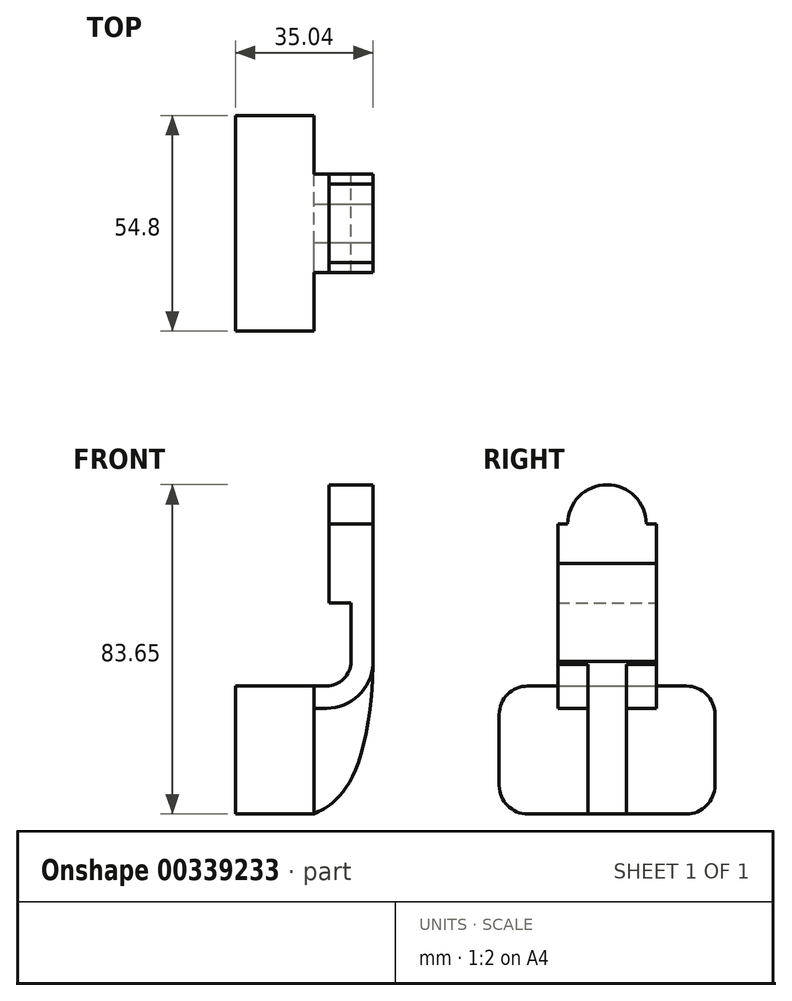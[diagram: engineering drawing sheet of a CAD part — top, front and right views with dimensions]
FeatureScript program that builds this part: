
annotation { "Feature Type Name" : "Feature", "Feature Type Description" : "" }
export const myFeature = defineFeature(function(context is Context, id is Id, definition is map)
    precondition{}
    {
        {
            var Q0;
            Q0=qCreatedBy(makeId("Front.planeOp"),FACE);
            var sketch = newSketch(context, id + "F0", { "sketchPlane" : qUnion([Q0])});
            skLineSegment(sketch, "E0.bottom", {"start": v(-10, 16.25) * mm, "end": v(10, 16.25) * mm});
            skLineSegment(sketch, "E0.top", {"start": v(-10, -16.25) * mm, "end": v(10, -16.25) * mm});
            skLineSegment(sketch, "E0.left", {"start": v(-10, 16.25) * mm, "end": v(-10, -16.25) * mm});
            skLineSegment(sketch, "E0.right", {"start": v(10, 16.25) * mm, "end": v(10, -16.25) * mm});
            skPoint(sketch, "E0.middle", {"position": v(0, 0) * mm});
            skLineSegment(sketch, "E1.bottom", {"start": v(13.75, 57.4) * mm, "end": v(25, 57.4) * mm});
            skLineSegment(sketch, "E1.top", {"start": v(13.75, 37.4) * mm, "end": v(25, 37.4) * mm});
            skLineSegment(sketch, "E1.left", {"start": v(13.75, 57.4) * mm, "end": v(13.75, 37.4) * mm});
            skLineSegment(sketch, "E1.right", {"start": v(25, 57.4) * mm, "end": v(25, 37.4) * mm});
            skPoint(sketch, "E1.middle", {"position": v(19.37, 47.4) * mm});
            skLineSegment(sketch, "E2", {"start": v(10, 16.25) * mm, "end": v(13.13, 16.25) * mm});
            skArc(sketch, "E3", {"start": v(13.13, 16.25) * mm, "mid": v(17.54, 18.08) * mm, "end": v(19.37, 22.5) * mm});
            skLineSegment(sketch, "E4", {"start": v(19.37, 22.5) * mm, "end": v(19.37, 47.4) * mm});
            skLineSegment(sketch, "E5.0", {"start": v(25.04, 22.5) * mm, "end": v(25.04, 47.4) * mm});
            skArc(sketch, "E5.1", {"start": v(13.13, 10.58) * mm, "mid": v(21.55, 14.07) * mm, "end": v(25.04, 22.5) * mm});
            skLineSegment(sketch, "E5.2", {"start": v(10, 10.58) * mm, "end": v(13.13, 10.58) * mm});
            skLineSegment(sketch, "E6", {"start": v(13.75, 47.4) * mm, "end": v(25.04, 47.4) * mm});
            skFitSpline(sketch, "E7", {"points": [v(10, -16.25) * mm, v(25.04, 22.5) * mm], "startDerivative": vector(11.57, 6.62) * mm, "endDerivative": vector(2.78, 102.06) * mm});
            skSolve(sketch);
        }
        {
            var Q0;
            {var subQ1=sQuery(id+"F0.wireOp",EDGE,"E0.bottom");Q0=makeQuery(id+"F0.imprint","IMPRINT",FACE,{"disambiguationData":[TD([[makeQuery(id+"F0.imprint","IMPRINT",EDGE,{"derivedFrom":subQ1}),-1.0]])]});}
            extrude(context, id + "F1", {"entities" : qUnion([Q0]), "endBound" : BoundingType.SYMMETRIC, "depth" : 54.8 * mm});
        }
        {
            var Q0;
            {var subQ9=sQuery(id+"F0.wireOp",EDGE,"E2");Q0=makeQuery(id+"F0.imprint","IMPRINT",FACE,{"disambiguationData":[TD([[makeQuery(id+"F0.imprint","IMPRINT",EDGE,{"derivedFrom":subQ9}),-1.0]])]});}
            var Q1;
            {var subQ1=sQuery(id+"F0.wireOp",EDGE,"E1.bottom");Q1=makeQuery(id+"F0.imprint","IMPRINT",FACE,{"disambiguationData":[TD([[makeQuery(id+"F0.imprint","IMPRINT",EDGE,{"derivedFrom":subQ1}),-1.0]])]});}
            var Q2;
            {var subQ0=sQuery(id+"F0.wireOp",EDGE,"E1.left");var subQ1=sQuery(id+"F0.wireOp",EDGE,"E1.top");var subQ2=makeQuery(id+"F0.imprint","INTERSECT",VERTEX,{"derivedFrom":[subQ1,subQ0]});Q2=makeQuery(id+"F0.imprint","IMPRINT",FACE,{"disambiguationData":[TD([[makeQuery(id+"F0.imprint","IMPRINT",EDGE,{"disambiguationData":[TD([[subQ2,-1.0]])],"derivedFrom":subQ1}),1.0]])]});}
            var Q3;
            {var subQ0=sQuery(id+"F0.wireOp",EDGE,"E1.right");var subQ1=sQuery(id+"F0.wireOp",EDGE,"E1.top");var subQ2=makeQuery(id+"F0.imprint","INTERSECT",VERTEX,{"derivedFrom":[subQ1,subQ0]});Q3=makeQuery(id+"F0.imprint","IMPRINT",FACE,{"disambiguationData":[TD([[makeQuery(id+"F0.imprint","IMPRINT",EDGE,{"disambiguationData":[TD([[subQ2,1.0]])],"derivedFrom":subQ1}),1.0]])]});}
            extrude(context, id + "F2", {"entities" : qUnion([Q0, Q1, Q2, Q3]), "operationType" : NewBodyOperationType.ADD, "endBound" : BoundingType.SYMMETRIC, "depth" : 25 * mm});
        }
        {
            var Q0;
            {var subQ3=sQuery(id+"F0.wireOp",EDGE,"E5.2");Q0=makeQuery(id+"F0.imprint","IMPRINT",FACE,{"disambiguationData":[TD([[makeQuery(id+"F0.imprint","IMPRINT",EDGE,{"derivedFrom":subQ3}),-1.0]])]});}
            extrude(context, id + "F3", {"entities" : qUnion([Q0]), "operationType" : NewBodyOperationType.ADD, "endBound" : BoundingType.SYMMETRIC, "depth" : 9.8 * mm});
        }
        {
            var Q0;
            {var subQ1=sQuery(id+"F0.wireOp",EDGE,"E1.bottom");Q0=makeQuery(id+"F0.imprint","IMPRINT",FACE,{"disambiguationData":[TD([[makeQuery(id+"F0.imprint","IMPRINT",EDGE,{"derivedFrom":subQ1}),-1.0]])]});}
            var Q1;
            Q1=sQuery(id+"F0.wireOp",EDGE,"E1.bottom");
            revolve(context, id + "F4", {"operationType" : NewBodyOperationType.ADD, "entities" : qUnion([Q0]), "axis" : qUnion([Q1]), "revolveType" : RevolveType.FULL});
        }
        {
            var Q0;
            Q0=makeQuery(id+"F1.opExtrude","CAP_EDGE",EDGE,{"disambiguationData":[OSD([sQuery(id+"F0.wireOp",EDGE,"E0.bottom")])],"isStart":true});
            var Q1;
            Q1=makeQuery(id+"F1.opExtrude","CAP_EDGE",EDGE,{"disambiguationData":[OSD([sQuery(id+"F0.wireOp",EDGE,"E0.top")])],"isStart":true});
            var Q2;
            Q2=makeQuery(id+"F1.opExtrude","CAP_EDGE",EDGE,{"disambiguationData":[OSD([sQuery(id+"F0.wireOp",EDGE,"E0.bottom")])],"isStart":false});
            var Q3;
            Q3=makeQuery(id+"F1.opExtrude","CAP_EDGE",EDGE,{"disambiguationData":[OSD([sQuery(id+"F0.wireOp",EDGE,"E0.top")])],"isStart":false});
            fillet(context, id + "F5", {"entities" : qUnion([Q0, Q1, Q2, Q3]), "radius" : 7.24 * mm, "tangentPropagation" : true, "allowEdgeOverflow" : false});
        }
    });
